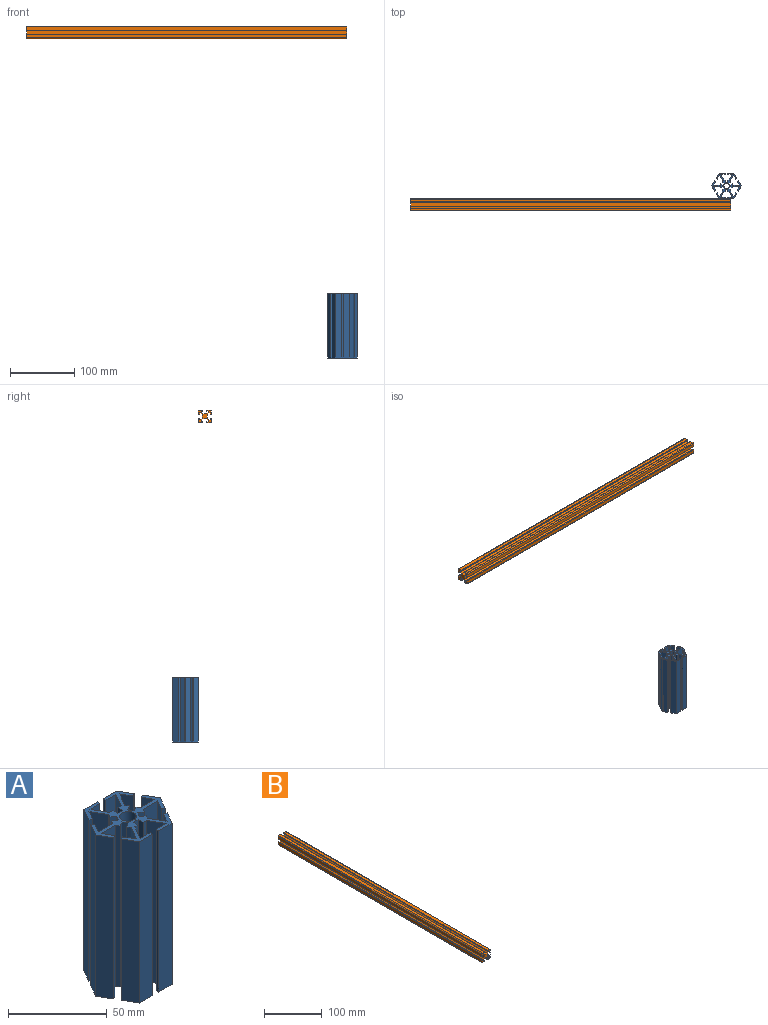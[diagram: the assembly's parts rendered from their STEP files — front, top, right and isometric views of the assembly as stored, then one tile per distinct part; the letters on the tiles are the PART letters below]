
ASSEMBLY  parts=2 mates=1
PART A: 81 faces, bbox 46.2x40x100 mm
  f0: plane 100x9mm, normal (0.87,0.5,0), area 1039.2mm2, adj f1,f77,f79,f80
  f1: plane 100x7.14mm, normal (0,-1,0), area 713.8mm2, adj f0,f2,f79,f80
  f2: plane 100x2mm, normal (1,0,0), area 200mm2, adj f1,f3,f79,f80
  f3: plane 100x9.45mm, normal (0,1,0), area 944.7mm2, adj f2,f4,f79,f80
  f4: plane 100x8.18mm, normal (-0.87,0.5,0), area 944.7mm2, adj f3,f5,f79,f80
  f5: plane 100x1.73mm, normal (-0.5,-0.87,0), area 200mm2, adj f4,f6,f79,f80
  f6: plane 100x6.18mm, normal (0.87,-0.5,0), area 713.8mm2, adj f5,f7,f79,f80
  f7: plane 100x9mm, normal (-0.87,-0.5,0), area 1039.2mm2, adj f6,f8,f79,f80
  f8: plane 100x1.98mm, normal (-0.87,0.5,0), area 229.1mm2, adj f7,f9,f79,f80
  f9: plane 100x3.03mm, normal (-0.5,-0.87,0), area 350mm2, adj f8,f10,f79,f80
  f10: plane 100x3.03mm, normal (-0.87,0.5,0), area 350mm2, adj f9,f11,f79,f80
  f11: plane 100x3.03mm, normal (0.5,0.87,0), area 350mm2, adj f10,f12,f79,f80
  f12: plane 100x1.98mm, normal (-0.87,0.5,0), area 229.1mm2, adj f11,f13,f79,f80
  f13: plane 100x10.39mm, normal (0,1,0), area 1039.2mm2, adj f12,f14,f79,f80
  f14: plane 100x6.18mm, normal (0.87,-0.5,0), area 713.8mm2, adj f13,f15,f79,f80
  f15: plane 100x1.73mm, normal (0.5,0.87,0), area 200mm2, adj f14,f16,f79,f80
  f16: plane 100x8.18mm, normal (-0.87,0.5,0), area 944.7mm2, adj f15,f17,f79,f80
  f17: plane 100x8.18mm, normal (-0.87,-0.5,0), area 944.7mm2, adj f16,f18,f79,f80
  f18: plane 100x1.73mm, normal (0.5,-0.87,0), area 200mm2, adj f17,f19,f79,f80
  f19: plane 100x6.18mm, normal (0.87,0.5,0), area 713.8mm2, adj f18,f20,f79,f80
  f20: plane 100x10.39mm, normal (0,-1,0), area 1039.2mm2, adj f19,f21,f79,f80
  f21: plane 100x1.98mm, normal (-0.87,-0.5,0), area 229.1mm2, adj f20,f22,f79,f80
  f22: plane 100x3.03mm, normal (0.5,-0.87,0), area 350mm2, adj f21,f23,f79,f80
  f23: plane 100x3.03mm, normal (-0.87,-0.5,0), area 350mm2, adj f22,f24,f79,f80
  f24: plane 100x3.03mm, normal (-0.5,0.87,0), area 350mm2, adj f23,f25,f79,f80
  f25: plane 100x1.98mm, normal (-0.87,-0.5,0), area 229.1mm2, adj f24,f26,f79,f80
  f26: plane 100x9mm, normal (-0.87,0.5,0), area 1039.2mm2, adj f25,f27,f79,f80
  f27: plane 100x6.18mm, normal (0.87,0.5,0), area 713.8mm2, adj f26,f28,f79,f80
  f28: plane 100x1.73mm, normal (-0.5,0.87,0), area 200mm2, adj f27,f29,f79,f80
  f29: plane 100x8.18mm, normal (-0.87,-0.5,0), area 944.7mm2, adj f28,f30,f79,f80
  f30: plane 100x9.45mm, normal (0,-1,0), area 944.7mm2, adj f29,f31,f79,f80
  f31: plane 100x2mm, normal (1,0,0), area 200mm2, adj f30,f32,f79,f80
  f32: plane 100x7.14mm, normal (0,1,0), area 713.8mm2, adj f31,f33,f79,f80
  f33: plane 100x9mm, normal (0.87,-0.5,0), area 1039.2mm2, adj f32,f34,f79,f80
  f34: plane 100x2.29mm, normal (0,-1,0), area 229.1mm2, adj f33,f35,f79,f80
  f35: plane 100x3.5mm, normal (1,0,0), area 350mm2, adj f34,f36,f79,f80
  f36: plane 100x3.5mm, normal (0,-1,0), area 350mm2, adj f35,f37,f79,f80
  f37: plane 100x3.5mm, normal (-1,0,0), area 350mm2, adj f36,f38,f79,f80
  f38: plane 100x2.29mm, normal (0,-1,0), area 229.1mm2, adj f37,f39,f79,f80
  f39: plane 100x9mm, normal (-0.87,-0.5,0), area 1039.2mm2, adj f38,f40,f79,f80
  f40: plane 100x7.14mm, normal (0,1,0), area 713.8mm2, adj f39,f41,f79,f80
  f41: plane 100x2mm, normal (-1,0,0), area 200mm2, adj f40,f42,f79,f80
  f42: plane 100x9.45mm, normal (0,-1,0), area 944.7mm2, adj f41,f43,f79,f80
  f43: plane 100x8.18mm, normal (0.87,-0.5,0), area 944.7mm2, adj f42,f44,f79,f80
  f44: plane 100x1.73mm, normal (0.5,0.87,0), area 200mm2, adj f43,f45,f79,f80
  f45: plane 100x6.18mm, normal (-0.87,0.5,0), area 713.8mm2, adj f44,f46,f79,f80
  f46: plane 100x9mm, normal (0.87,0.5,0), area 1039.2mm2, adj f45,f47,f79,f80
  f47: plane 100x1.98mm, normal (0.87,-0.5,0), area 229.1mm2, adj f46,f48,f79,f80
  f48: plane 100x3.03mm, normal (0.5,0.87,0), area 350mm2, adj f47,f49,f79,f80
  f49: plane 100x3.03mm, normal (0.87,-0.5,0), area 350mm2, adj f48,f50,f79,f80
  f50: plane 100x3.03mm, normal (-0.5,-0.87,0), area 350mm2, adj f49,f51,f79,f80
  f51: plane 100x1.98mm, normal (0.87,-0.5,0), area 229.1mm2, adj f50,f52,f79,f80
  f52: plane 100x10.39mm, normal (0,-1,0), area 1039.2mm2, adj f51,f53,f79,f80
  f53: plane 100x6.18mm, normal (-0.87,0.5,0), area 713.8mm2, adj f52,f54,f79,f80
  f54: plane 100x1.73mm, normal (-0.5,-0.87,0), area 200mm2, adj f53,f55,f79,f80
  f55: plane 100x8.18mm, normal (0.87,-0.5,0), area 944.7mm2, adj f54,f56,f79,f80
  f56: plane 100x8.18mm, normal (0.87,0.5,0), area 944.7mm2, adj f55,f57,f79,f80
  f57: plane 100x1.73mm, normal (-0.5,0.87,0), area 200mm2, adj f56,f58,f79,f80
  f58: plane 100x6.18mm, normal (-0.87,-0.5,0), area 713.8mm2, adj f57,f59,f79,f80
  f59: plane 100x10.39mm, normal (0,1,0), area 1039.2mm2, adj f58,f60,f79,f80
  f60: plane 100x1.98mm, normal (0.87,0.5,0), area 229.1mm2, adj f59,f61,f79,f80
  f61: plane 100x3.03mm, normal (-0.5,0.87,0), area 350mm2, adj f60,f62,f79,f80
  f62: plane 100x3.03mm, normal (0.87,0.5,0), area 350mm2, adj f61,f63,f79,f80
  f63: plane 100x3.03mm, normal (0.5,-0.87,0), area 350mm2, adj f62,f64,f79,f80
  f64: plane 100x1.98mm, normal (0.87,0.5,0), area 229.1mm2, adj f63,f65,f79,f80
  f65: plane 100x9mm, normal (0.87,-0.5,0), area 1039.2mm2, adj f64,f66,f79,f80
  f66: plane 100x6.18mm, normal (-0.87,-0.5,0), area 713.8mm2, adj f65,f67,f79,f80
  f67: plane 100x1.73mm, normal (0.5,-0.87,0), area 200mm2, adj f66,f68,f79,f80
  f68: plane 100x8.18mm, normal (0.87,0.5,0), area 944.7mm2, adj f67,f69,f79,f80
  f69: plane 100x9.45mm, normal (0,1,0), area 944.7mm2, adj f68,f70,f79,f80
  f70: plane 100x2mm, normal (-1,0,0), area 200mm2, adj f69,f71,f79,f80
  f71: plane 100x7.14mm, normal (0,-1,0), area 713.8mm2, adj f70,f72,f79,f80
  f72: plane 100x9mm, normal (-0.87,0.5,0), area 1039.2mm2, adj f71,f73,f79,f80
  f73: plane 100x2.29mm, normal (0,1,0), area 229.1mm2, adj f72,f74,f79,f80
  f74: plane 100x3.5mm, normal (-1,0,0), area 350mm2, adj f73,f75,f79,f80
  f75: plane 100x3.5mm, normal (0,1,0), area 350mm2, adj f74,f76,f79,f80
  f76: plane 100x3.5mm, normal (1,0,0), area 350mm2, adj f75,f77,f79,f80
  f77: plane 100x2.29mm, normal (0,1,0), area 229.1mm2, adj f0,f76,f79,f80
  f78: cylinder r=4.25mm len=100mm, axis (0,0,-1), area 2670.4mm2, adj f79,f80
  f79: plane 46.19x40mm, normal (0,0,1), area 487.9mm2, adj f0,f1,f2,f3,f4,f5,f6,f7
  f80: plane 46.19x40mm, normal (0,0,-1), area 487.9mm2, adj f0,f1,f2,f3,f4,f5,f6,f7
PART B: 50 faces, bbox 20x500x20 mm
  f0: plane 500x1.78mm, normal (-1,0,0), area 889mm2, adj f1,f43,f44,f45
  f1: plane 500x5.39mm, normal (0,0,-1), area 2694.3mm2, adj f0,f44,f45,f46
  f2: plane 500x5.39mm, normal (1,0,0), area 2694.2mm2, adj f3,f44,f45,f46
  f3: plane 500x1.78mm, normal (0,0,1), area 889mm2, adj f2,f4,f44,f45
  f4: plane 500x2.35mm, normal (-1,0,0), area 1174.7mm2, adj f3,f5,f44,f45
  f5: plane 500x1.78mm, normal (0,0,1), area 889mm2, adj f4,f6,f44,f45
  f6: plane 500x2.67mm, normal (0.66,0,0.75), area 1777.1mm2, adj f5,f7,f44,f45
  f7: plane 500x6.22mm, normal (1,0,0), area 3111.5mm2, adj f6,f8,f44,f45
  f8: plane 500x2.67mm, normal (0.66,0,-0.75), area 1777.1mm2, adj f7,f9,f44,f45
  f9: plane 500x1.78mm, normal (0,0,-1), area 889mm2, adj f8,f10,f44,f45
  f10: plane 500x2.35mm, normal (-1,0,0), area 1174.7mm2, adj f9,f11,f44,f45
  f11: plane 500x1.78mm, normal (0,0,-1), area 889mm2, adj f10,f12,f44,f45
  f12: plane 500x5.39mm, normal (1,0,0), area 2694.3mm2, adj f11,f44,f45,f47
  f13: plane 500x5.39mm, normal (0,0,1), area 2694.2mm2, adj f14,f44,f45,f47
  f14: plane 500x1.78mm, normal (-1,0,0), area 889mm2, adj f13,f15,f44,f45
  f15: plane 500x2.35mm, normal (0,0,-1), area 1174.7mm2, adj f14,f16,f44,f45
  f16: plane 500x1.78mm, normal (-1,0,0), area 889mm2, adj f15,f17,f44,f45
  f17: plane 500x2.67mm, normal (-0.75,0,0.66), area 1777.1mm2, adj f16,f18,f44,f45
  f18: plane 500x6.22mm, normal (0,0,1), area 3111.5mm2, adj f17,f19,f44,f45
  f19: plane 500x2.67mm, normal (0.75,0,0.66), area 1777.1mm2, adj f18,f20,f44,f45
  f20: plane 500x1.78mm, normal (1,0,0), area 889mm2, adj f19,f21,f44,f45
  f21: plane 500x2.35mm, normal (0,0,-1), area 1174.7mm2, adj f20,f22,f44,f45
  f22: plane 500x1.78mm, normal (1,0,0), area 889mm2, adj f21,f23,f44,f45
  f23: plane 500x5.39mm, normal (0,0,1), area 2694.3mm2, adj f22,f44,f45,f48
  f24: plane 500x5.39mm, normal (-1,0,0), area 2694.2mm2, adj f25,f44,f45,f48
  f25: plane 500x1.78mm, normal (0,0,-1), area 889mm2, adj f24,f26,f44,f45
  f26: plane 500x2.35mm, normal (1,0,0), area 1174.7mm2, adj f25,f27,f44,f45
  f27: plane 500x1.78mm, normal (0,0,-1), area 889mm2, adj f26,f28,f44,f45
  f28: plane 500x2.67mm, normal (-0.66,0,-0.75), area 1777.1mm2, adj f27,f29,f44,f45
  f29: plane 500x6.22mm, normal (-1,0,0), area 3111.5mm2, adj f28,f30,f44,f45
  f30: plane 500x2.67mm, normal (-0.66,0,0.75), area 1777.1mm2, adj f29,f31,f44,f45
  f31: plane 500x1.78mm, normal (0,0,1), area 889mm2, adj f30,f32,f44,f45
  f32: plane 500x2.35mm, normal (1,0,0), area 1174.7mm2, adj f31,f33,f44,f45
  f33: plane 500x1.78mm, normal (0,0,1), area 889mm2, adj f32,f34,f44,f45
  f34: plane 500x5.39mm, normal (-1,0,0), area 2694.3mm2, adj f33,f44,f45,f49
  f35: plane 500x5.39mm, normal (0,0,-1), area 2694.3mm2, adj f36,f44,f45,f49
  f36: plane 500x1.78mm, normal (1,0,0), area 889mm2, adj f35,f37,f44,f45
  f37: plane 500x2.35mm, normal (0,0,1), area 1174.7mm2, adj f36,f38,f44,f45
  f38: plane 500x1.78mm, normal (1,0,0), area 889mm2, adj f37,f39,f44,f45
  f39: plane 500x2.67mm, normal (0.75,0,-0.66), area 1777.1mm2, adj f38,f40,f44,f45
  f40: plane 500x6.22mm, normal (0,0,-1), area 3111.5mm2, adj f39,f41,f44,f45
  f41: plane 500x2.67mm, normal (-0.75,0,-0.66), area 1777.1mm2, adj f40,f42,f44,f45
  f42: plane 500x1.78mm, normal (-1,0,0), area 889mm2, adj f41,f43,f44,f45
  f43: plane 500x2.35mm, normal (0,0,1), area 1174.7mm2, adj f0,f42,f44,f45
  f44: plane 20x20mm, normal (0,-1,0), area 184.7mm2, adj f0,f1,f2,f3,f4,f5,f6,f7
  f45: plane 20x20mm, normal (0,1,0), area 184.7mm2, adj f0,f1,f2,f3,f4,f5,f6,f7
  f46: cylinder r=1.5mm len=500mm, axis (0,1,0), area 1178.1mm2, adj f1,f2,f44,f45
  f47: cylinder r=1.5mm len=500mm, axis (0,-1,0), area 1178.1mm2, adj f12,f13,f44,f45
  f48: cylinder r=1.5mm len=500mm, axis (0,1,0), area 1178.1mm2, adj f23,f24,f44,f45
  f49: cylinder r=1.5mm len=500mm, axis (0,-1,0), area 1178.1mm2, adj f34,f35,f44,f45
PLACE A at identity
PLACE B rot(axis=(-0.71,0.71,0),180deg) t=(-493.18,-30,508.5)mm
MATE parallel B.f24 <-> A.f42  axis (0,1,0) through (6.82,-20,500)mm
